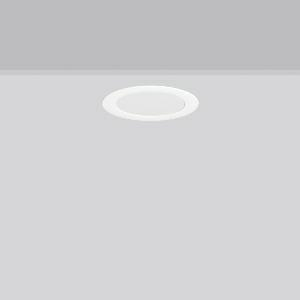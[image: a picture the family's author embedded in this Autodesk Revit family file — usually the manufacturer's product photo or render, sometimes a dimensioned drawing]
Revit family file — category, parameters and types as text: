
# Revit family: toledo_flat_round_e_672222_002_04_7e31
name_source: partatom
category: Lighting Fixtures
units: mm (PartAtom-declared; Revit-internal decimal feet)

## family parameters
Cut with Voids When Loaded = No
Host = Face
Light Source = No
Part Type = Normal
Room Calculation Point = No
Round Connector Dimension = Use Diameter
Shared = No

## types (1)
- TOLEDO FLAT round E (1 x LED Modul 830, 780 lm, 3000)
    Apparent Load = 8 VA
    CIE Flux Codes = 47 79 96 100 100
    Color Rendering = 80
    Color Temperature = 3000
    Default Elevation = 1800 mm
    Description = Series: TOLEDO FLAT round
Ultra thin recessed downlight. For escape route illumination. Housing: die-cast aluminium, powder-coated. Lightguide and diffuser made of non-yellowing plastic (PMMA). Diffuser opal matt plastic. Ceiling installation with spring system. Including separate LED converter with connecting cable 250 mm. Self-contained system with automatic self-test and feedback to the RZB monitoring system MULTIDIGIT. External driver with simple plug-in locking system. 
Colour: white
Diameter: 190 mm
Height: 2.5 mm
Cut-out diameter: 170 mm
Recess height: 120 mm
Luminaire: recess height: 60-80 mm
Weight: 1.41 kg
Operating mode: maintained power mode
Duration time: 3 h
Lamp: LED
Socket: without socket
Colour temperature: 3000K
Colour rendering index (CRI): 80
System power: 7.7 W
Rated luminous flux: 780 lm
Luminous flux, emergency: 350 lm
System power, emergency: -
Control gear: Regulated power supply
Protection class: I
Type of protection: IP 54
    Height = 0 mm  [stored 0 ft]
    Lamp = 1 x LED Modul 830
    Lamp Light Flux = 780 lm
    Lamp count = 1
    Length = 190 mm  [stored 0.62336 ft]
    Lifetime = 50000 h
    Luminous efficacy = 101 lm/W
    Manufacturer = RZB
    ModVariant = No
    Model = 672222.002.04
    Mounting Place = Ceiling
    Mounting Type = Recessed
    Number of Poles = 1
    OnlyDefault = Yes
    Power Factor = 1
    Product Name = TOLEDO FLAT round E
    Product group = Recessed downlights
    ProductGroupID = 402
    Protection Class = Protection class I
    Protection Degree = IP 40
    RLX_Detail_Level = 1
    RLX_Emergency_Light_Flux = 350 lm
    RLX_Emergency_Type = 3
    RLX_Emergency_Type_DB = Yes
    RlxData = <blob elided: 29361 chars, md5=5ec224db>
    Socket = socket
    Standby Power = 0 W
    System Light Flux = 780 lm
    System Power = 8 W
    Type Comments = Product without accessories
    Type Image = 901452.002.jpg
    URL = http://relux.com
    VarID = ---
    Voltage = 230 V
    Voltage Range = 220-240 V
    Weight = 0.00 kg
    Width = 0 mm  [stored 0 ft]

note: [stored X ft] marks values corroborated as IEEE doubles in the binary element streams (Revit-internal decimal feet)

## geometry (parser evidence)
native form markers: Blend x4, Sweep x10
no freeform markers — native parametric forms only
